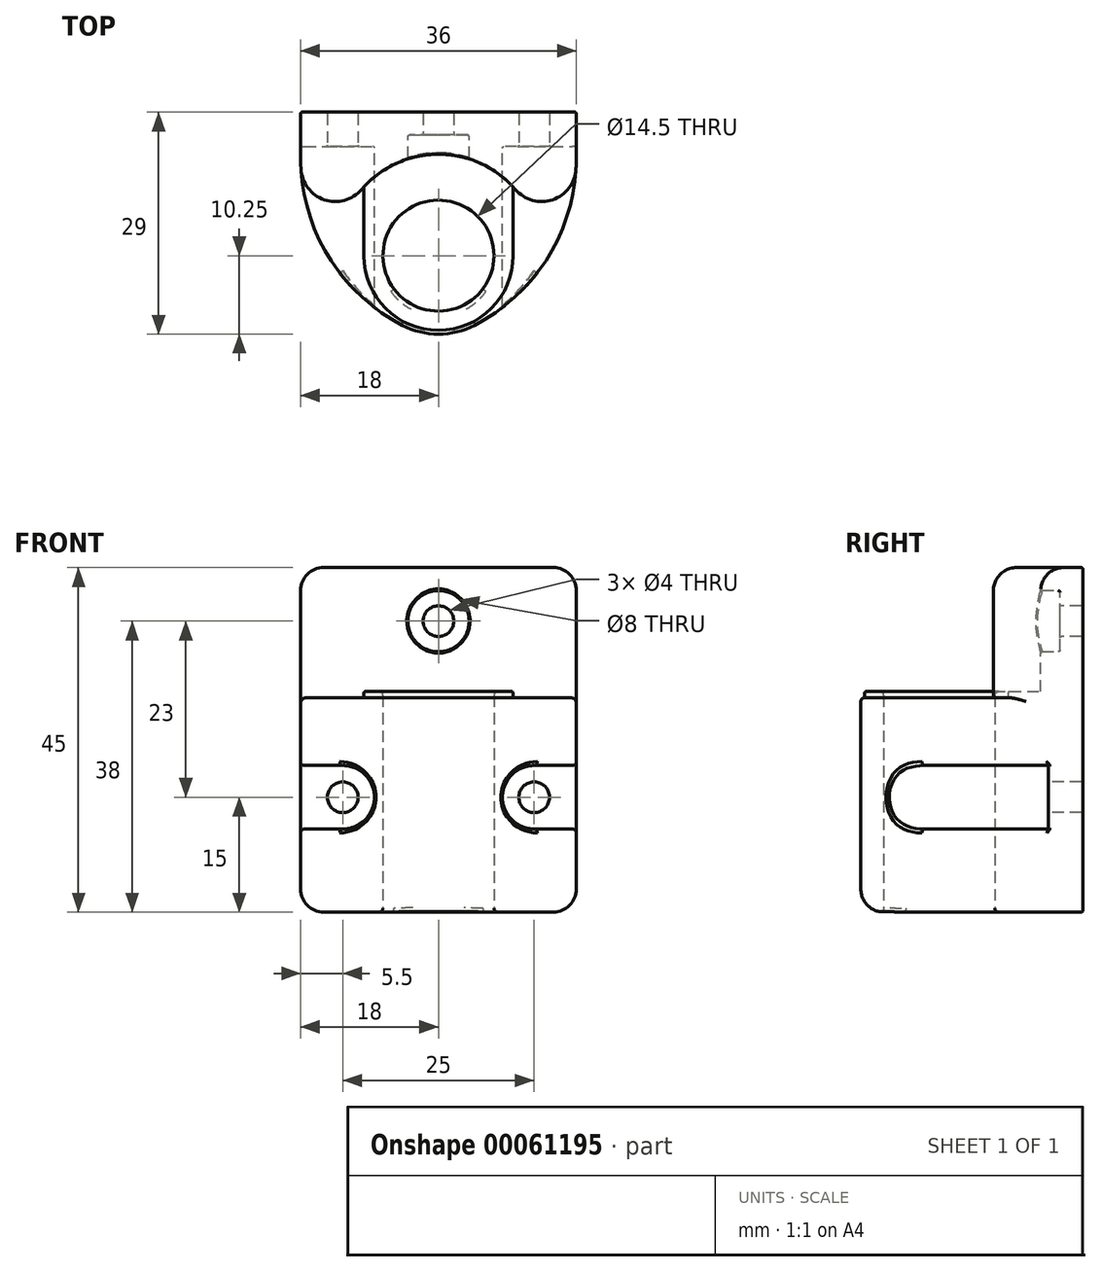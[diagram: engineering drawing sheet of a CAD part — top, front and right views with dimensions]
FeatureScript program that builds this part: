
annotation { "Feature Type Name" : "Feature", "Feature Type Description" : "" }
export const myFeature = defineFeature(function(context is Context, id is Id, definition is map)
    precondition{}
    {
        {
            var Q0;
            Q0=qCreatedBy(makeId("Top.planeOp"),FACE);
            var sketch = newSketch(context, id + "F0", { "sketchPlane" : qUnion([Q0])});
            skLineSegment(sketch, "E0", {"start": v(-18, 0) * mm, "end": v(18, 0) * mm});
            skPoint(sketch, "E1", {"position": v(0, 0) * mm});
            skLineSegment(sketch, "E2", {"start": v(-18, 0) * mm, "end": v(-18, -6) * mm});
            skLineSegment(sketch, "E3", {"start": v(18, 0) * mm, "end": v(18, -6) * mm});
            skLineSegment(sketch, "E4", {"start": v(0, 0) * mm, "end": v(0, -29) * mm, "construction": true});
            skCircle(sketch, "E5", {"center": v(0, -18.75) * mm, "radius": 7.25 * mm});
            skArc(sketch, "E6", {"start": v(-18, -6) * mm, "mid": v(-14.42, -18.78) * mm, "end": v(-4.72, -27.85) * mm});
            skArc(sketch, "E7", {"start": v(4.72, -27.85) * mm, "mid": v(14.42, -18.78) * mm, "end": v(18, -6) * mm});
            skArc(sketch, "E8", {"start": v(-4.72, -27.85) * mm, "mid": v(0, -29) * mm, "end": v(4.72, -27.85) * mm});
            skArc(sketch, "E9", {"start": v(4.72, -27.85) * mm, "mid": v(0, -8.5) * mm, "end": v(-4.72, -27.85) * mm, "construction": true});
            skSolve(sketch);
        }
        {
            var Q0;
            Q0 = qSketchRegion(id + "F0", true);
            extrude(context, id + "F1", {"entities" : qUnion([Q0]), "depth" : 45 * mm});
        }
        {
            var Q0;
            Q0=makeQuery(id+"F1.opExtrude","CAP_FACE",FACE,{"disambiguationData":[OSD([sQuery(id+"F0.wireOp",EDGE,"E0"),sQuery(id+"F0.wireOp",EDGE,"E2"),sQuery(id+"F0.wireOp",EDGE,"E3"),sQuery(id+"F0.wireOp",EDGE,"E5"),sQuery(id+"F0.wireOp",EDGE,"E6"),sQuery(id+"F0.wireOp",EDGE,"E7"),sQuery(id+"F0.wireOp",EDGE,"E8")])],"isStart":false});
            var sketch = newSketch(context, id + "F2", { "sketchPlane" : qUnion([Q0])});
            skCircle(sketch, "E10", {"center": v(0, -18.75) * mm, "radius": 13.25 * mm});
            skSolve(sketch);
        }
        {
            var Q0;
            Q0 = qSketchRegion(id + "F2", true);
            extrude(context, id + "F3", {"entities" : qUnion([Q0]), "operationType" : NewBodyOperationType.REMOVE, "oppositeDirection" : true, "depth" : 17 * mm});
        }
        {
            var Q0;
            Q0=makeQuery(id+"F3.boolean.opBoolean","INTERSECT",EDGE,{"derivedFrom":[makeQuery(id+"F1.opExtrude","SWEPT_FACE",FACE,{"disambiguationData":[OSD([sQuery(id+"F0.wireOp",EDGE,"E6")])]}),makeQuery(id+"F3.opExtrude","SWEPT_FACE",FACE,{"disambiguationData":[OSD([sQuery(id+"F2.wireOp",EDGE,"E10")])]})]});
            var Q1;
            Q1=makeQuery(id+"F3.boolean.opBoolean","INTERSECT",EDGE,{"derivedFrom":[makeQuery(id+"F1.opExtrude","SWEPT_FACE",FACE,{"disambiguationData":[OSD([sQuery(id+"F0.wireOp",EDGE,"E7")])]}),makeQuery(id+"F3.opExtrude","SWEPT_FACE",FACE,{"disambiguationData":[OSD([sQuery(id+"F2.wireOp",EDGE,"E10")])]})]});
            fillet(context, id + "F4", {"entities" : qUnion([Q0, Q1]), "radius" : 4.5 * mm, "tangentPropagation" : true, "allowEdgeOverflow" : false});
        }
        {
            var Q0;
            Q0=makeQuery(id+"F3.boolean.opBoolean","COPY",FACE,{"derivedFrom":makeQuery(id+"F3.opExtrude","CAP_FACE",FACE,{"disambiguationData":[OSD([sQuery(id+"F2.wireOp",EDGE,"E10")])],"isStart":false})});
            var sketch = newSketch(context, id + "F5", { "sketchPlane" : qUnion([Q0])});
            skLineSegment(sketch, "E11", {"start": v(-9.75, -18.75) * mm, "end": v(-9.75, -9.78) * mm});
            skLineSegment(sketch, "E12", {"start": v(9.75, -18.75) * mm, "end": v(9.75, -9.78) * mm});
            skArc(sketch, "E13", {"start": v(-9.75, -18.75) * mm, "mid": v(0, -28.5) * mm, "end": v(9.75, -18.75) * mm});
            skArc(sketch, "E14", {"start": v(9.75, -18.75) * mm, "mid": v(0, -9) * mm, "end": v(-9.75, -18.75) * mm, "construction": true});
            skArc(sketch, "E15", {"start": v(9.75, -9.78) * mm, "mid": v(0, -5.5) * mm, "end": v(-9.75, -9.78) * mm});
            skCircle(sketch, "E16.0", {"center": v(0, -18.75) * mm, "radius": 7.25 * mm});
            skSolve(sketch);
        }
        {
            var Q0;
            Q0 = qSketchRegion(id + "F5", true);
            extrude(context, id + "F6", {"entities" : qUnion([Q0]), "operationType" : NewBodyOperationType.ADD, "depth" : .8 * mm});
        }
        {
            var Q0;
            Q0=qCreatedBy(makeId("Front.planeOp"),FACE);
            cPlane(context, id + "F7", {"entities" : qUnion([Q0]), "cplaneType" : CPlaneType.OFFSET, "offset" : 4.5 * mm, "width" : 150 * mm, "height" : 150 * mm});
        }
        {
            var Q0;
            Q0=qCreatedBy(id+"F7.planeOp",FACE);
            var sketch = newSketch(context, id + "F8", { "sketchPlane" : qUnion([Q0])});
            skLineSegment(sketch, "E17", {"start": v(12.5, 19.15) * mm, "end": v(18, 19.15) * mm});
            skLineSegment(sketch, "E18", {"start": v(18, 19.15) * mm, "end": v(18, 10.85) * mm});
            skLineSegment(sketch, "E19", {"start": v(18, 10.85) * mm, "end": v(12.5, 10.85) * mm});
            skArc(sketch, "E20", {"start": v(12.5, 19.15) * mm, "mid": v(8.35, 15) * mm, "end": v(12.5, 10.85) * mm});
            skArc(sketch, "E21", {"start": v(12.5, 10.85) * mm, "mid": v(16.65, 15) * mm, "end": v(12.5, 19.15) * mm, "construction": true});
            skLineSegment(sketch, "E22.MirrorCS", {"start": v(-12.5, 19.15) * mm, "end": v(-18, 19.15) * mm});
            skLineSegment(sketch, "E23.MirrorCS", {"start": v(-18, 19.15) * mm, "end": v(-18, 10.85) * mm});
            skLineSegment(sketch, "E24.MirrorCS", {"start": v(-18, 10.85) * mm, "end": v(-12.5, 10.85) * mm});
            skArc(sketch, "E25.MirrorCS", {"start": v(-12.5, 19.15) * mm, "mid": v(-8.35, 15) * mm, "end": v(-12.5, 10.85) * mm});
            skArc(sketch, "E26.MirrorCS", {"start": v(-12.5, 10.85) * mm, "mid": v(-16.65, 15) * mm, "end": v(-12.5, 19.15) * mm, "construction": true});
            skSolve(sketch);
        }
        {
            var Q0;
            Q0 = qSketchRegion(id + "F8", true);
            extrude(context, id + "F9", {"entities" : qUnion([Q0]), "operationType" : NewBodyOperationType.REMOVE, "depth" : 25 * mm});
        }
        {
            var Q0;
            Q0=makeQuery(id+"F9.boolean.opBoolean","COPY",FACE,{"derivedFrom":makeQuery(id+"F9.opExtrude","CAP_FACE",FACE,{"disambiguationData":[OSD([sQuery(id+"F8.wireOp",EDGE,"E17"),sQuery(id+"F8.wireOp",EDGE,"E18"),sQuery(id+"F8.wireOp",EDGE,"E19"),sQuery(id+"F8.wireOp",EDGE,"E20")])],"isStart":true})});
            var sketch = newSketch(context, id + "F10", { "sketchPlane" : qUnion([Q0])});
            skCircle(sketch, "E27", {"center": v(12.5, 15) * mm, "radius": 2 * mm});
            skCircle(sketch, "E28", {"center": v(-12.5, 15) * mm, "radius": 2 * mm});
            skPoint(sketch, "E29", {"position": v(18, 15) * mm});
            skSolve(sketch);
        }
        {
            var Q0;
            Q0 = qSketchRegion(id + "F10", true);
            extrude(context, id + "F11", {"entities" : qUnion([Q0]), "operationType" : NewBodyOperationType.REMOVE, "oppositeDirection" : true, "depth" : 25 * mm});
        }
        {
            var Q0;
            Q0=qCreatedBy(id+"F7.planeOp",FACE);
            var sketch = newSketch(context, id + "F12", { "sketchPlane" : qUnion([Q0])});
            skCircle(sketch, "E30", {"center": v(0, 38) * mm, "radius": 4 * mm});
            skSolve(sketch);
        }
        {
            var Q0;
            Q0 = qSketchRegion(id + "F12", true);
            extrude(context, id + "F13", {"entities" : qUnion([Q0]), "operationType" : NewBodyOperationType.REMOVE, "endBound" : BoundingType.THROUGH_ALL, "depth" : 25 * mm, "hasSecondDirection" : true, "secondDirectionOppositeDirection" : true, "secondDirectionDepth" : 1.5 * mm});
        }
        {
            var Q0;
            Q0=makeQuery(id+"F13.boolean.opBoolean","COPY",FACE,{"derivedFrom":makeQuery(id+"F13.opExtrude","CAP_FACE",FACE,{"disambiguationData":[OSD([sQuery(id+"F12.wireOp",EDGE,"E30")])],"isStart":true})});
            var sketch = newSketch(context, id + "F14", { "sketchPlane" : qUnion([Q0])});
            skCircle(sketch, "E31", {"center": v(0, 38) * mm, "radius": 2 * mm});
            skSolve(sketch);
        }
        {
            var Q0;
            Q0 = qSketchRegion(id + "F14", true);
            extrude(context, id + "F15", {"entities" : qUnion([Q0]), "operationType" : NewBodyOperationType.REMOVE, "endBound" : BoundingType.THROUGH_ALL, "oppositeDirection" : true, "depth" : 25 * mm});
        }
        {
            var Q0;
            Q0=makeQuery(id+"F1.opExtrude","CAP_EDGE",EDGE,{"disambiguationData":[OSD([sQuery(id+"F0.wireOp",EDGE,"E3")])],"isStart":true});
            var Q1;
            Q1=makeQuery(id+"F1.opExtrude","CAP_EDGE",EDGE,{"disambiguationData":[OSD([sQuery(id+"F0.wireOp",EDGE,"E3")])],"isStart":false});
            fillet(context, id + "F16", {"entities" : qUnion([Q0, Q1]), "radius" : 3 * mm, "tangentPropagation" : true, "allowEdgeOverflow" : false});
        }
        {
            var Q0;
            Q0=makeQuery(id+"F9.boolean.opBoolean","INTERSECT",EDGE,{"derivedFrom":[makeQuery(id+"F1.opExtrude","SWEPT_FACE",FACE,{"disambiguationData":[OSD([sQuery(id+"F0.wireOp",EDGE,"E7")])]}),makeQuery(id+"F9.opExtrude","SWEPT_FACE",FACE,{"disambiguationData":[OSD([sQuery(id+"F8.wireOp",EDGE,"E19")])]})]});
            var Q1;
            Q1=makeQuery(id+"F9.boolean.opBoolean","INTERSECT",EDGE,{"derivedFrom":[makeQuery(id+"F1.opExtrude","SWEPT_FACE",FACE,{"disambiguationData":[OSD([sQuery(id+"F0.wireOp",EDGE,"E6")])]}),makeQuery(id+"F9.opExtrude","SWEPT_FACE",FACE,{"disambiguationData":[OSD([sQuery(id+"F8.wireOp",EDGE,"E24.MirrorCS")])]})]});
            var Q2;
            Q2=makeQuery(id+"F9.boolean.opBoolean","COPY",EDGE,{"derivedFrom":makeQuery(id+"F9.opExtrude","CAP_EDGE",EDGE,{"disambiguationData":[OSD([sQuery(id+"F8.wireOp",EDGE,"E18")])],"isStart":true})});
            var Q3;
            Q3=makeQuery(id+"F9.boolean.opBoolean","COPY",EDGE,{"derivedFrom":makeQuery(id+"F9.opExtrude","CAP_EDGE",EDGE,{"disambiguationData":[OSD([sQuery(id+"F8.wireOp",EDGE,"E23.MirrorCS")])],"isStart":true})});
            fillet(context, id + "F17", {"entities" : qUnion([Q0, Q1, Q2, Q3]), "radius" : 0.5 * mm, "tangentPropagation" : true, "allowEdgeOverflow" : false});
        }
        {
            var Q0;
            Q0=makeQuery(id+"F3.boolean.opBoolean","INTERSECT",EDGE,{"derivedFrom":[makeQuery(id+"F1.opExtrude","SWEPT_FACE",FACE,{"disambiguationData":[OSD([sQuery(id+"F0.wireOp",EDGE,"E6")])]}),makeQuery(id+"F3.opExtrude","CAP_FACE",FACE,{"disambiguationData":[OSD([sQuery(id+"F2.wireOp",EDGE,"E10")])],"isStart":false})]});
            fillet(context, id + "F18", {"entities" : qUnion([Q0]), "radius" : .5 * mm, "tangentPropagation" : true, "allowEdgeOverflow" : false});
        }
        {
            var Q0;
            Q0=makeQuery(id+"F6.opExtrude","CAP_EDGE",EDGE,{"disambiguationData":[OSD([sQuery(id+"F5.wireOp",EDGE,"E16.0")])],"isStart":false});
            var Q1;
            Q1=makeQuery(id+"F1.opExtrude","CAP_EDGE",EDGE,{"disambiguationData":[OSD([sQuery(id+"F0.wireOp",EDGE,"E5")])],"isStart":true});
            fillet(context, id + "F19", {"entities" : qUnion([Q0, Q1]), "radius" : .5 * mm, "tangentPropagation" : true, "allowEdgeOverflow" : false});
        }
        {
            var Q0;
            Q0=makeQuery(id+"F13.boolean.opBoolean","INTERSECT",EDGE,{"derivedFrom":[makeQuery(id+"F3.boolean.opBoolean","COPY",FACE,{"derivedFrom":makeQuery(id+"F3.opExtrude","SWEPT_FACE",FACE,{"disambiguationData":[OSD([sQuery(id+"F2.wireOp",EDGE,"E10")])]})}),makeQuery(id+"F13.opExtrude","SWEPT_FACE",FACE,{"disambiguationData":[OSD([sQuery(id+"F12.wireOp",EDGE,"E30")])]})]});
            var Q1;
            Q1=makeQuery(id+"F1.opExtrude","SWEPT_FACE",FACE,{"disambiguationData":[OSD([sQuery(id+"F0.wireOp",EDGE,"E0")])]});
            var Q2;
            Q2=makeQuery(id+"F6.opExtrude","CAP_EDGE",EDGE,{"disambiguationData":[OSD([sQuery(id+"F5.wireOp",EDGE,"E12")])],"isStart":false});
            var Q3;
            Q3=makeQuery(id+"F9.boolean.opBoolean","COPY",FACE,{"derivedFrom":makeQuery(id+"F9.opExtrude","CAP_FACE",FACE,{"disambiguationData":[OSD([sQuery(id+"F8.wireOp",EDGE,"E17"),sQuery(id+"F8.wireOp",EDGE,"E18"),sQuery(id+"F8.wireOp",EDGE,"E19"),sQuery(id+"F8.wireOp",EDGE,"E20")])],"isStart":true})});
            var Q4;
            Q4=makeQuery(id+"F9.boolean.opBoolean","COPY",FACE,{"derivedFrom":makeQuery(id+"F9.opExtrude","CAP_FACE",FACE,{"disambiguationData":[OSD([sQuery(id+"F8.wireOp",EDGE,"E22.MirrorCS"),sQuery(id+"F8.wireOp",EDGE,"E23.MirrorCS"),sQuery(id+"F8.wireOp",EDGE,"E24.MirrorCS"),sQuery(id+"F8.wireOp",EDGE,"E25.MirrorCS")])],"isStart":true})});
            var Q5;
            Q5=makeQuery(id+"F13.boolean.opBoolean","COPY",FACE,{"derivedFrom":makeQuery(id+"F13.opExtrude","CAP_FACE",FACE,{"disambiguationData":[OSD([sQuery(id+"F12.wireOp",EDGE,"E30")])],"isStart":true})});
            fillet(context, id + "F20", {"entities" : qUnion([Q0, Q1, Q2, Q3, Q4, Q5]), "radius" : .2 * mm, "tangentPropagation" : true, "allowEdgeOverflow" : false});
        }
    });
